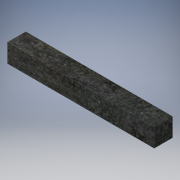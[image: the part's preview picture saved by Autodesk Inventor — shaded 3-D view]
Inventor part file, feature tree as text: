
AUTODESK INVENTOR PART (.ipt)
format: ipt  version: 2019 (Build 230136000, 136)  size: 107,520 bytes
history: native  units: mm
features: extrude x1, sketch x1
ambient origin geometry x8: Origin, YZ Plane, XZ Plane, XY Plane, X Axis, Y Axis, Z Axis, Center Point
bodies: Solid1 (feature_tree)
feature tree (2):
  extrude  "Extrusion1"  Depth=10.0mm
  sketch  "Sketch1"  dims[d0=80.0mm d1=10.0mm d4=75.0mm d5=15.0mm d6=10.0mm d7=0.0mm]
